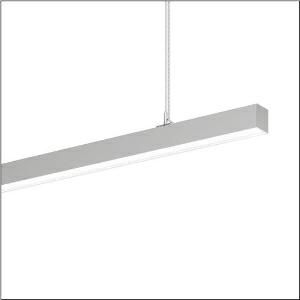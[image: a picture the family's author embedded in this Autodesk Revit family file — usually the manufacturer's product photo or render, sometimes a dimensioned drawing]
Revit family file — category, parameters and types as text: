
# Revit family: silica_21_51mx30da44sb
name_source: partatom
category: Lighting Fixtures
units: mm (PartAtom-declared; Revit-internal decimal feet)

## family parameters
Cut with Voids When Loaded = No
Host = Face
Light Source = No
Part Type = Normal
Room Calculation Point = No
Round Connector Dimension = Use Diameter
Shared = No

## types (1)
- --- (1 x LED, 4210 lm, 26 W, 4000K)
    Apparent Load = 26 VA
    CIE Flux Codes = 47 79 96 57 100
    Color Rendering = 80
    Color Temperature = 4000K
    Default Elevation = 1800 mm
    Description = Silica 21, office luminaire, primary optical cover: cover, of PMMA, opal, light emission: direct/indirect distribution, primary light characteristic: symmetric, installation type: suspended mounting, LED, rated luminous flux: 4.210lm, luminous efficacy: 162lm/W, light colour: 840, colour temperature: 4000K, control gear: DALI 2, with terminal, 3+2-pole, max. 2.5mm², mains connection: 220..240V, AC, 50/60Hz, rated input power: 26W, luminaire housing, of aluminium, metallic grey (RAL 9006), length: 1.204mm, width: 53mm, height: 53mm, protection rating (complete): IP20, insulation class (complete): insulation class I (protective earthing), certification: CE, permissible operating ambient temperature: 0..+35°C, standard: EN 50419, packaging unit: 1 piece
    Height = 53 mm
    Lamp = 1 x LED
    Lamp Light Flux = 4210 lm
    Lamp Power = 26 W
    Lamp count = 1
    Length = 1204 mm
    Luminous efficacy = 162 lm/W
    Manufacturer = Siteco
    ModVariant = No
    Model = 51MX30DA44SB
    Mounting Place = Ceiling
    Mounting Type = Pendant
    Number of Poles = 1
    OnlyDefault = Yes
    Power Factor = 1
    Product Name = Silica 21
    Product group = office luminaire | ceiling pendant
    ProductGroupID = 903
    Protection Class = Protection class I
    Protection Degree = IP 20
    RLX_Detail_Level = 1
    RLX_Emergency_Light_Flux = 0 lm
    RLX_Emergency_Type = 0
    RLX_Emergency_Type_DB = No
    RlxData = <blob elided: 23157 chars, md5=9f9ea24b>
    Socket = socket
    Standby Power = 0 W
    System Light Flux = 4210 lm
    System Power = 26 W
    Type Comments = factory setting: luminous flux: 100 % | dim-lin: 254 | 218 mA
    Type Image = l_1335864.jpg
    URL = http://relux.com
    VarID = @adj_118909
    Voltage = 0 V
    Weight = 0.00 kg
    Width = 53 mm

## geometry (parser evidence)
native form markers: Blend x4, Sweep x11
no freeform markers — native parametric forms only
